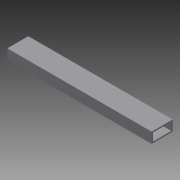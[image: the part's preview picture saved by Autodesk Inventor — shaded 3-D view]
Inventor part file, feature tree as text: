
AUTODESK INVENTOR PART (.ipt)
format: ipt  version: 2013 (Build 170138000, 138)  size: 78,336 bytes
history: native  units: in
note: dims shown in document units (in); Inventor stores cm internally (conversion verified against a paired STEP export)
features: extrude x2, sketch x2
ambient origin geometry x8: Origin, YZ Plane, XZ Plane, XY Plane, X Axis, Y Axis, Z Axis, Center Point
bodies: Solid1 (feature_tree)
feature tree (4):
  extrude  "Extrusion1"  Depth=2.0in
  extrude  "Extrusion2"  Depth=0.125in
  sketch  "Sketch1"  dims[d0=13.75in d1=2.0in]
  sketch  "Sketch2"  dims[d2=1.0in d3=0.0in d4=0.125in d5=0.125in d6=1.75in d7=0.75in d8=20.0in d9=0.0in]
